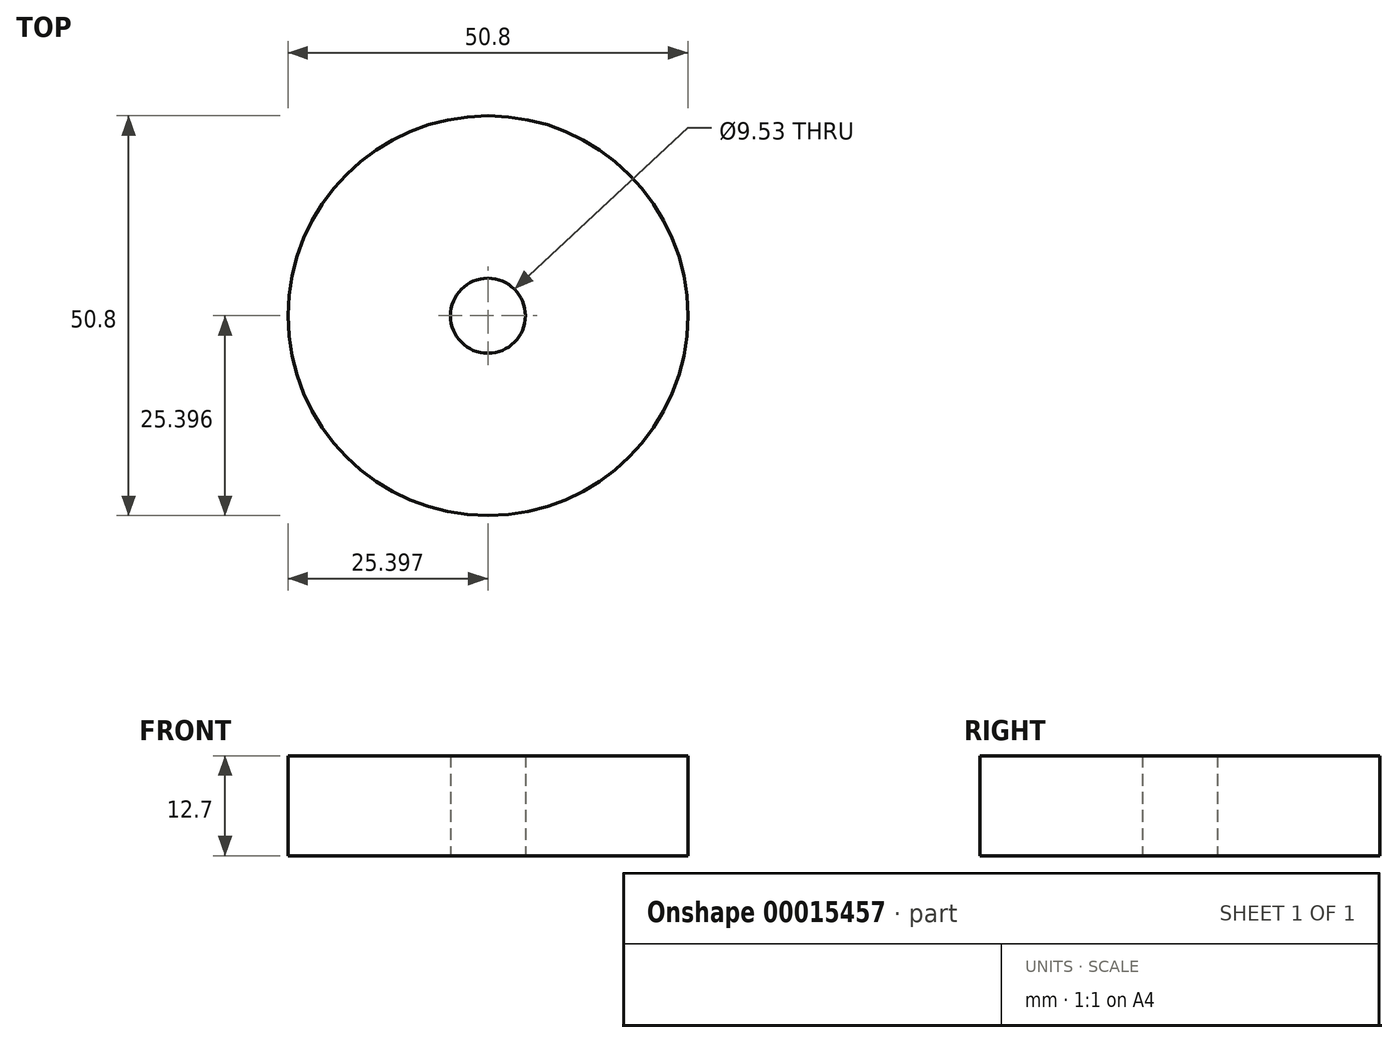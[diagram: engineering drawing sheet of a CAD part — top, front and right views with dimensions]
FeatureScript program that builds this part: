
annotation { "Feature Type Name" : "Feature", "Feature Type Description" : "" }
export const myFeature = defineFeature(function(context is Context, id is Id, definition is map)
    precondition{}
    {
        {
            var Q0;
            Q0=qCreatedBy(makeId("Top.planeOp"),FACE);
            var sketch = newSketch(context, id + "F0", { "sketchPlane" : qUnion([Q0])});
            skCircle(sketch, "E0", {"center": v(-12.92, 23.1) * mm, "radius": 25.4 * mm});
            skCircle(sketch, "E1", {"center": v(-12.92, 23.1) * mm, "radius": 4.76 * mm});
            skSolve(sketch);
        }
        {
            var Q0;
            Q0=makeQuery(id+"F0.imprint","IMPRINT",FACE,{"disambiguationData":[TD([[makeQuery(id+"F0.imprint","IMPRINT",EDGE,{"derivedFrom":sQuery(id+"F0.wireOp",EDGE,"E0")}),1.0]])]});
            extrude(context, id + "F1", {"entities" : qUnion([Q0]), "depth" : 12.7 * mm});
        }
    });
